# Revit family: S1617 updated
name_source: partatom
category: Lighting Fixtures
units: mm (PartAtom-declared; Revit-internal decimal feet)

## family parameters
Cut with Voids When Loaded = No
Host = Face
Light Source = No
Part Type = Normal
Room Calculation Point = No
Round Connector Dimension = Use Diameter
Shared = Yes

## types (4) — shared parameters
Current Amps = 50 A
Default Elevation = 48 "
Description = Flexible, Linear LED Lighting
Environment = Indoor
Frequency = 60 Hz
Has Battery Backup = No
Has Dimming = Yes
Housing Protection Rating = Consult Manufacturer Website for more Information
Initial Intensity Comments = Refer LED Strip type for Lumen Value
Input Voltage = 24VDC
LED Tape Documentation link = https://bllighting.com
LED finish = LED
LED strip = Strip
Lamp Life = 50,000 Hours
Lens Material = Polycarbonate Optic
Load Classification = Lighting
Manufacturer = BL Lighting
Mounting Method = Surface Mount
Number of Poles = 1
Operating Temperature = Consult Manufacturer Website for more Information
Phase = 1
Power Factor = 1
Power Source Type = Driver
Product Documentation Link = https://bllighting.com
Product Page URL = https://bllighting.com
Profile Material = Alumnium Base Track
URL = https://bllighting.com
Version = 2020-v2.9
Voltage = 24 V
W = 0.67 "
Warranty URL = https://bllighting.com

## per-type parameters (varying)
| type | Apparent Load | CCT | Color Option Available | DFD1 | DFD2 | DFD3 | DFRGBW 2 | Increment | Initial Color Comments | LED Tape Page URL | Lumen Output | Max Input Current | Model | Number of LED's | Product Name | Wattage Comments |
| 105 lm per FT 1.22W per FT - DFD1 | 96 VA | 2700K,3000K,4000K,6500K | 2700K,3000K,4000K,6500K | Yes | No | No | No | 1.9685 " | Perfomance based on 2700K Photometric Web File | https://bllighting.com | 105 lm/FT | 4A | DFD1 | 146 Diodes/FT | DFD1 | 1.22W/FT |
| 207 lm per FT 4.57 W per FT - DFRGBW 2 | 15 VA | 3000K | 3000K | No | No | No | Yes | 3.2795 " | Perfomance based on 3000K Photometric Web File | https://bllighting.com | 207 lm/FT | 0.625A | DFRGBW 2 | 410 Diodes/FT | DFRGBW 2 | 4.57W/FT |
| 258 lm per FT 2.44 W per FT - DFD2 | 96 VA | 2400K,2700K,3000K,3500K,4000K | 2400K,2700K,3000K,3500K,4000K | No | Yes | No | No | 1.9685 " | Perfomance based on 3000K Photometric Web File | https://blhttps:
lighting.com/products/led-tape/dfd1 | 258 lm/FT | 4A | DFD2 | 146 Diodes/FT | DFD2 | 2.44W/FT |
| 419 lm per FT 4.4 W per FT - DFD3 | 96 VA | 2400K,2700K,3000K,3500K,4000K | 2400K,2700K,3000K,3500K,4000K | No | No | Yes | No | 1.9685 " | Perfomance based on 3000K Photometric Web File | https://bllighting.com | 421 lm/FT | 4A | DFD3 | 146 Diodes/FT | DFD3 | 4.4W/FT |

## geometry (parser evidence)
native form markers: Sweep x39
no freeform markers — native parametric forms only
